# Revit family: IS_Conca_T3952_BIM_IT
name_source: partatom
category: Plumbing Fixtures
revit_build: Autodesk Revit 2017 (Build: 20160225_1515(x64)
units: mm (PartAtom-declared; Revit-internal decimal feet)

## family parameters
Always vertical = No
Cut with Voids When Loaded = No
OmniClass Number = 23.45.05.14.21.11
OmniClass Title = Bath/Shower Units
Part Type = Normal
Room Calculation Point = No
Round Connector Dimension = Use Diameter
Shared = No
Work Plane-Based = No

## types (6) — shared parameters
Accessori = https://www.idealstandard.it
Aiuto = https://www.idealstandard.it
AltezzaNominale = 80 mm  [stored 0.262467 ft]
Autore = Ideal Standard
BIMobject category = Storage
BIMobject category code = sanitary-storage
BIMobject main category = Sanitary
BIMobject main category code = sanitary
Brand = https://www.idealstandard.it
DescrizioneClassifcazioneUni2015 = Bathroom cabinets
DurataGaranzia = 2
DurataGaranziaProdotti = 2
Forma = Rettangolare
Garanzia = Garanzia Idealstandard
IfcEsportaCome = IfcFurnitureType
InformaziniGaranzia = https://www.idealstandard.it
InformazioniDiProdotto = http://www.idealstandard.it
InformazioniGaranzia = https://www.idealstandard.it
Installation instructions = https://www.idealspec.co.uk
InstruzioniInstallazione = https://www.idealstandard.it
LarghezzaNominale = 1200 mm
Maniglia = No
Manufacturer = Ideal Standard
Materiale = Ceramics
NominalDepth = 505 mm  [stored 1.65682 ft]
NominalHeight = 80 mm  [stored 0.262467 ft]
NominalWidth = 1200 mm
PesoNetto = 11.5
PiattoDoccia = No
Product group = Bathroom_Furniture
Produttore = Ideal Standard
ProfonditaNominale = 505 mm  [stored 1.65682 ft]
Revisione = 1
RiferimentoClassificazioneUni2015 = Pr_40_30_78_03
Spazio = Interno
Telefono = 800 652 290
TipoEspotazioneIfc = Bathroom cabinets
URL = https://www.ideal-standard.co.uk
Uniclass 2015 Code = Pr_40_30_78_03
Uniclass 2015 Name = Bathroom cabinets
UnitàDurata = Anno
UnitàDurataGaranzia = Anno
UnitàLineare = Milimitre
UnitàMonetaria = €
UnitàSuperficie = Milimitre
UnitàVolume = Litri
Versione = 1
VersioneClassificazioneUni2015 = v1.1
zero-valued in all types: CostoDiSostituzione, DimensioneScarico, LunghezzaNominale, Nominal depth, Nominal height, SeatMaterial, SpessoreDelMateriale, SpilloverLivello, Weight Net (Kg)

## per-type parameters (varying)
| type | Caratteristiche | CodiceABarre | CodiceArticolo | Colore | Description | Desrizione | Finitura | Model | ModelloDiRiferimento | Nome | NomeOggettoBim | NumeroDiModello |
| T3952Y1 - Conca CONSOLE 120X50  WHMT - T3952 - Y1_MattWhite | Mensola in truciolare nobilitato1200 x 505 x 80 mm. Da abbinare alle staffe di fissaggio (U842867) da acquistare separatamente. La mensola viene fornita senza taglio. Finitura Bianco laccato opaco | 8014140461456 | T3952Y1 | Matt white | Console, 1200 x 505 x 80 mm. To be combined with the fixing brackets (U842867) to be purchased separately. The shelf is supplied without cutting. Matt white lacquered finish | Mensola in truciolare nobilitato1200 x 505 x 80 mm. Da abbinare alle staffe di fissaggio (U842867) da acquistare separatamente. La mensola viene fornita senza taglio. Finitura Bianco laccato opaco | Matt white | T3952Y1 | T3952Y1 | BathroomCabinets_Conca_T3952Y1_IdealStandard | ISI_IdealStandard_Bathroom Cabinets_Conca_T3952Y1 | T3952Y1 |
| T3952Y2 - Conca CONSOLE 120X50  WHMT - T3952 - Y2_MattAntracite | Mensola in truciolare nobilitato1200 x 505 x 80 mm. Da abbinare alle staffe di fissaggio (U842867) da acquistare separatamente. La mensola viene fornita senza taglio. Finitura Antracite laccato opaco | 8014140461463 | T3952Y2 | Matt anthracite | Console, 1200 x 505 x 80 mm. To be combined with the fixing brackets (U842867) to be purchased separately. The shelf is supplied without cutting. Anthracite matt lacquer finish | Mensola in truciolare nobilitato1200 x 505 x 80 mm. Da abbinare alle staffe di fissaggio (U842867) da acquistare separatamente. La mensola viene fornita senza taglio. Finitura Antracite laccato opaco | Matt anthracite | T3952Y2 | T3952Y2 | BathroomCabinets_Conca_T3952Y2_IdealStandard | ISI_IdealStandard_Bathroom Cabinets_Conca_T3952Y2 | T3952Y2 |
| T3952Y3 - Conca CONSOLE 120X50  WHMT - T3952 - Y3_MattSunset | Mensola in truciolare nobilitato1200 x 505 x 80 mm. Da abbinare alle staffe di fissaggio (U842867) da acquistare separatamente. La mensola viene fornita senza taglio. Finitura Sunset laccato opaco | 8014140461470 | T3952Y3 | Matt Sunset | Console, 1200 x 505 x 80 mm. To be combined with the fixing brackets (U842867) to be purchased separately. The shelf is supplied without cutting. Sunset matt lacquer finish | Mensola in truciolare nobilitato1200 x 505 x 80 mm. Da abbinare alle staffe di fissaggio (U842867) da acquistare separatamente. La mensola viene fornita senza taglio. Finitura Sunset laccato opaco | Matt Sunset | T3952Y3 | T3952Y3 | BathroomCabinets_Conca_T3952Y3_IdealStandard | ISI_IdealStandard_Bathroom Cabinets_Conca_T3952Y3 | T3952Y3 |
| T3952Y4 - Conca CONSOLE 120X50  WHMT - T3952 - Y4_SmokedOak | Mensola in truciolare nobilitato1200 x 505 x 80 mm. Da abbinare alle staffe di fissaggio (U842867) da acquistare separatamente. La mensola viene fornita senza taglio. Finitura Rovere affumicato scuro | 8014140461487 | T3952Y4 | Smoked Oak | Console, 1200 x 505 x 80 mm. To be combined with the fixing brackets (U842867) to be purchased separately. The shelf is supplied without cutting. Dark smoked oak finish | Mensola in truciolare nobilitato1200 x 505 x 80 mm. Da abbinare alle staffe di fissaggio (U842867) da acquistare separatamente. La mensola viene fornita senza taglio. Finitura Rovere affumicato scuro | Smoked Oak | T3952Y4 | T3952Y4 | BathroomCabinets_Conca_T3952Y4_IdealStandard | ISI_IdealStandard_Bathroom Cabinets_Conca_T3952Y4 | T3952Y4 |
| T3952Y5 - Conca CONSOLE 120X50  WHMT - T3952 - Y5_DarkWalnut | Mensola in truciolare nobilitato1200 x 505 x 80 mm. Da abbinare alle staffe di fissaggio (U842867) da acquistare separatamente. La mensola viene fornita senza taglio. Finitura Noce scuro | 8014140461494 | T3952Y5 | Dark Walnut | Console, 1200 x 505 x 80 mm. To be combined with the fixing brackets (U842867) to be purchased separately. The shelf is supplied without cutting. Dark Walnut finish | Mensola in truciolare nobilitato1200 x 505 x 80 mm. Da abbinare alle staffe di fissaggio (U842867) da acquistare separatamente. La mensola viene fornita senza taglio. Finitura Noce scuro | Dark Walnut | T3952Y5 | T3952Y5 | BathroomCabinets_Conca_T3952Y5_IdealStandard | ISI_IdealStandard_Bathroom Cabinets_Conca_T3952Y5 | T3952Y5 |
| T3952Y6 - Conca CONSOLE 120X50  WHMT - T3952 - Y6_LightOak | Mensola in truciolare nobilitato1200 x 505 x 80 mm. Da abbinare alle staffe di fissaggio (U842867) da acquistare separatamente. La mensola viene fornita senza taglio. Finitura Legno chiaro | 8014140461500 | T3952Y6 | Light Oak | Console, 1200 x 505 x 80 mm. To be combined with the fixing brackets (U842867) to be purchased separately. The shelf is supplied without cutting. Light wood finish | Mensola in truciolare nobilitato1200 x 505 x 80 mm. Da abbinare alle staffe di fissaggio (U842867) da acquistare separatamente. La mensola viene fornita senza taglio. Finitura Legno chiaro | Light Oak | T3952Y6 | T3952Y6 | BathroomCabinets_Conca_T3952Y6_IdealStandard | ISI_IdealStandard_Bathroom Cabinets_Conca_T3952Y6 | T3952Y6 |

note: [stored X ft] marks values corroborated as IEEE doubles in the binary element streams (Revit-internal decimal feet)

## geometry (parser evidence)
native form markers: Sweep x3
no freeform markers — native parametric forms only
